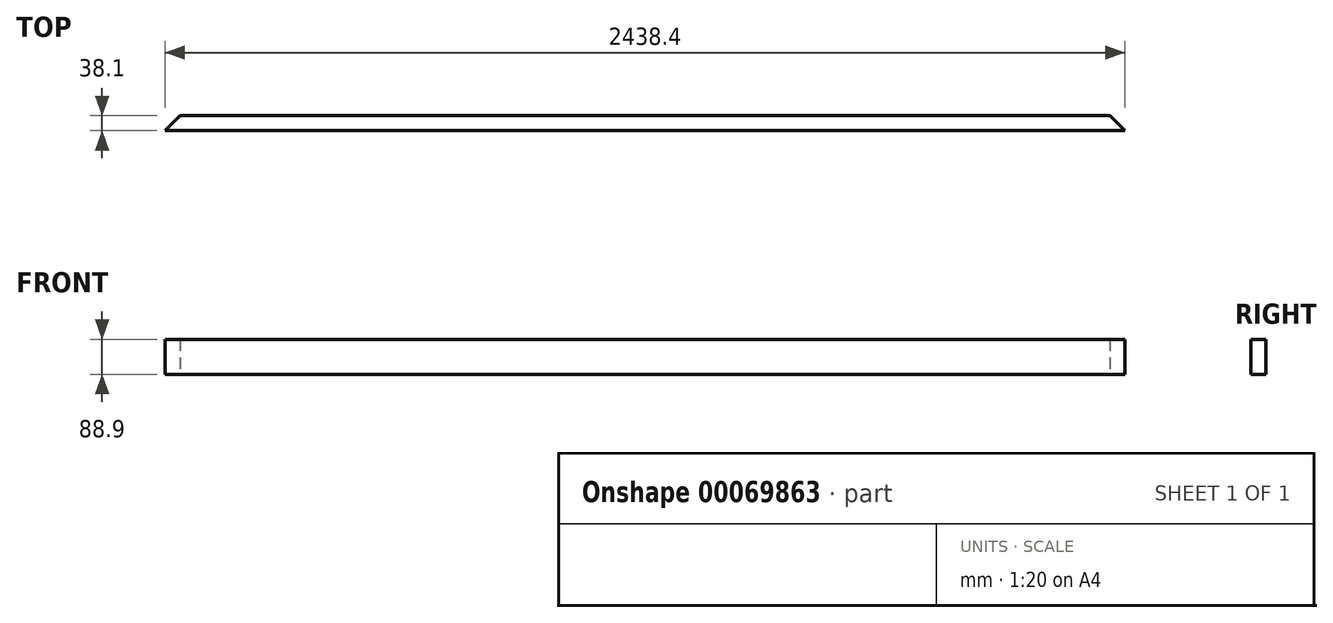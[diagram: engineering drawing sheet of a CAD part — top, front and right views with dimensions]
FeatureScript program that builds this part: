
annotation { "Feature Type Name" : "Feature", "Feature Type Description" : "" }
export const myFeature = defineFeature(function(context is Context, id is Id, definition is map)
    precondition{}
    {
        {
            var Q0;
            Q0=qCreatedBy(makeId("Top.planeOp"),FACE);
            var sketch = newSketch(context, id + "F2", { "sketchPlane" : qUnion([Q0])});
            skLineSegment(sketch, "E0.rect.bottom", {"start": v(1181.1, 19.05) * mm, "end": v(-1181.1, 19.05) * mm});
            skLineSegment(sketch, "E0.rect.top", {"start": v(1219.2, -19.05) * mm, "end": v(-1219.2, -19.05) * mm});
            skPoint(sketch, "E0.rect.middle", {"position": v(0, 0) * mm});
            skLineSegment(sketch, "E1", {"start": v(1219.2, -19.05) * mm, "end": v(1181.1, 19.05) * mm});
            skLineSegment(sketch, "E2", {"start": v(-1219.2, -19.05) * mm, "end": v(-1181.1, 19.05) * mm});
            skPoint(sketch, "E0.rect.left.start.orphan", {"position": v(1219.2, 19.05) * mm});
            skPoint(sketch, "E0.rect.right.start.orphan", {"position": v(-1219.2, 19.05) * mm});
            skSolve(sketch);
        }
        {
            var Q0;
            Q0=makeQuery(id+"F2.imprint","IMPRINT",FACE,{"disambiguationData":[TD([[makeQuery(id+"F2.imprint","IMPRINT",EDGE,{"derivedFrom":sQuery(id+"F2.wireOp",EDGE,"E0.rect.bottom")}),1.0]])]});
            extrude(context, id + "F0", {"entities" : qUnion([Q0]), "depth" : 88.9 * mm});
        }
    });
